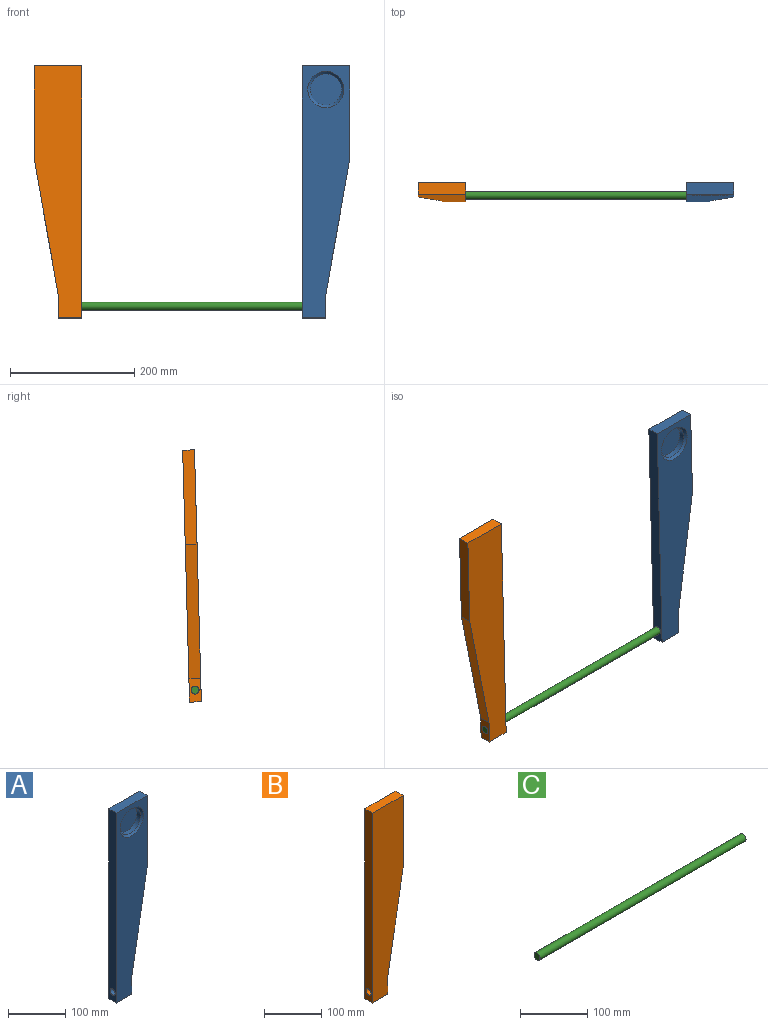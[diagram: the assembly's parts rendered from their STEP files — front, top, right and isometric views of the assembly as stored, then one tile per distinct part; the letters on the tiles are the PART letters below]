
ASSEMBLY  parts=3 mates=5
PART A: 12 faces, bbox 76.2x19.1x406.4 mm
  f0: plane 406.4x19.05mm, normal (-1,0,0), area 7615.2mm2, adj f1,f5,f6,f7,f11
  f1: plane 38.1x19.05mm, normal (0,0,-1), area 725.8mm2, adj f0,f2,f6,f7
  f2: plane 38.1x19.05mm, normal (1,0,0), area 599.1mm2, adj f1,f3,f6,f7,f11
  f3: plane 215.9x38.1mm, normal (0.98,0,-0.17), area 4176.4mm2, adj f2,f4,f6,f7
  f4: plane 152.4x19.05mm, normal (1,0,0), area 2903.2mm2, adj f3,f5,f6,f7
  f5: plane 76.2x19.05mm, normal (0,0,1), area 1451.6mm2, adj f0,f4,f6,f7
  f6: plane 406.4x76.2mm, normal (0,-1,0), area 22722.7mm2, adj f0,f1,f2,f3,f4,f5,f10
  f7: plane 406.4x76.2mm, normal (0,1,0), area 25403.2mm2, adj f0,f1,f2,f3,f4,f5
  f8: cylinder r=25.4mm len=50.8mm, axis (0,-1,0), area 1418.8mm2, adj f9,f10
  f9: plane 50.8x50.8mm, normal (0,-1,0), area 2026.8mm2, adj f8
  f10: cone r=25.4mm half-angle=45deg, axis (0,-1,0), area 924.4mm2, adj f6,f8
  f11: cylinder r=6.35mm len=38.1mm, axis (-1,0,0), area 1520.1mm2, adj f0,f2
PART B: 9 faces, bbox 76.2x19.1x406.4 mm
  f0: plane 406.4x19.05mm, normal (-1,0,0), area 7615.2mm2, adj f1,f5,f6,f7,f8
  f1: plane 38.1x19.05mm, normal (0,0,-1), area 725.8mm2, adj f0,f2,f6,f7
  f2: plane 38.1x19.05mm, normal (1,0,0), area 599.1mm2, adj f1,f3,f6,f7,f8
  f3: plane 215.9x38.1mm, normal (0.98,0,-0.17), area 4176.4mm2, adj f2,f4,f6,f7
  f4: plane 152.4x19.05mm, normal (1,0,0), area 2903.2mm2, adj f3,f5,f6,f7
  f5: plane 76.2x19.05mm, normal (0,0,1), area 1451.6mm2, adj f0,f4,f6,f7
  f6: plane 406.4x76.2mm, normal (0,-1,0), area 25403.2mm2, adj f0,f1,f2,f3,f4,f5
  f7: plane 406.4x76.2mm, normal (0,1,0), area 25403.2mm2, adj f0,f1,f2,f3,f4,f5
  f8: cylinder r=6.35mm len=38.1mm, axis (1,0,0), area 1520.1mm2, adj f0,f2
PART C: 3 faces, bbox 431.8x12.7x12.7 mm
  f0: cylinder r=6.35mm len=431.8mm, axis (-1,0,0), area 17228.1mm2, adj f1,f2
  f1: plane 12.7x12.7mm, normal (1,0,0), area 126.7mm2, adj f0
  f2: plane 12.7x12.7mm, normal (-1,0,0), area 126.7mm2, adj f0
PLACE A rot(axis=(-1,0,0),1.6deg) t=(393.7,9,-19.3)mm
PLACE B rot(axis=(0,0.01,1),180deg) t=(38.1,-10.04,-18.78)mm
PLACE C at identity fixed
MATE cylindrical A.f11 <-> C.f0  axis (-1,0,0) through (431.8,0,0)mm
MATE cylindrical C.f0 <-> B.f8  axis (-1,0,0) through (0,0,0)mm
MATE parallel B.f7 <-> A.f6  axis (0,-1,0.03) through (5.2,-3.82,209.93)mm
MATE planar C.f0 <-> A.f11  axis (1,0,0) through (431.8,0,0)mm
MATE planar B.f8 <-> C.f0  axis (-1,0,0) through (0,0,0)mm
